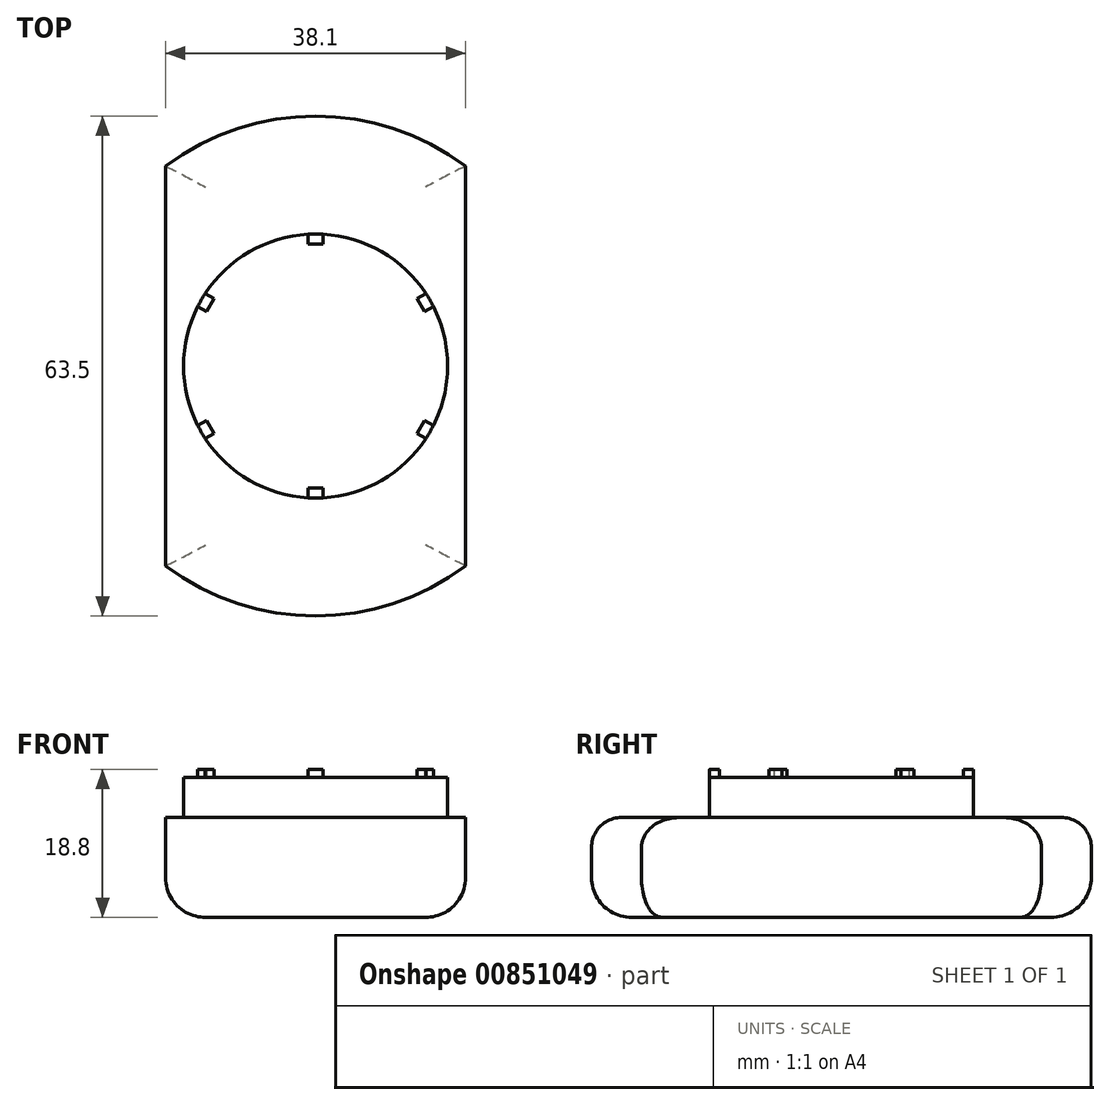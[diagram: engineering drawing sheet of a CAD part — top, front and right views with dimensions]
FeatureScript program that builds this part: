
annotation { "Feature Type Name" : "Feature", "Feature Type Description" : "" }
export const myFeature = defineFeature(function(context is Context, id is Id, definition is map)
    precondition{}
    {
        {
            var Q0;
            Q0=qCreatedBy(makeId("Top.planeOp"),FACE);
            var sketch = newSketch(context, id + "F0", { "sketchPlane" : qUnion([Q0])});
            skCircle(sketch, "E0", {"center": v(0, 0) * mm, "radius": 16.76 * mm});
            skLineSegment(sketch, "E1", {"start": v(-0.95, 16.74) * mm, "end": v(-0.95, 15.47) * mm});
            skLineSegment(sketch, "E2", {"start": v(-0.95, 15.47) * mm, "end": v(0.95, 15.47) * mm});
            skLineSegment(sketch, "E3", {"start": v(0.95, 15.47) * mm, "end": v(0.95, 16.74) * mm});
            skLineSegment(sketch, "E4", {"start": v(0, 0) * mm, "end": v(0, 15.47) * mm, "construction": true});
            skSolve(sketch);
        }
        {
            var Q0;
            Q0 = qSketchRegion(id + "F0", true);
            extrude(context, id + "F1", {"entities" : qUnion([Q0]), "oppositeDirection" : true, "depth" : 5.08 * mm, "offsetDistance" : 25.4 * mm});
        }
        {
            var Q0;
            {var subQ0=sQuery(id+"F0.wireOp",EDGE,"E1");Q0=makeQuery(id+"F0.imprint","IMPRINT",FACE,{"disambiguationData":[TD([[makeQuery(id+"F0.imprint","IMPRINT",EDGE,{"derivedFrom":subQ0}),1.0]])]});}
            extrude(context, id + "F2", {"entities" : qUnion([Q0]), "depth" : 1.02 * mm, "offsetDistance" : 25.4 * mm});
        }
        {
            var Q0;
            Q0=makeQuery(id+"F2.opExtrude","SWEPT_BODY",BODY,{"disambiguationData":[OSD([sQuery(id+"F0.wireOp",EDGE,"E0"),sQuery(id+"F0.wireOp",EDGE,"E1"),sQuery(id+"F0.wireOp",EDGE,"E2"),sQuery(id+"F0.wireOp",EDGE,"E3")])]});
            var Q1;
            Q1=sQuery(id+"F0.wireOp",EDGE,"E0");
            circularPattern(context, id + "F3", {"entities" : qUnion([Q0]), "axis" : qUnion([Q1]), "angle" : 360 * degree, "instanceCount" : 6, "equalSpace" : true});
        }
        {
            var Q0;
            Q0=makeQuery(id+"F1.opExtrude","CAP_FACE",FACE,{"disambiguationData":[OSD([sQuery(id+"F0.wireOp",EDGE,"E0")])],"isStart":false});
            var sketch = newSketch(context, id + "F4", { "sketchPlane" : qUnion([Q0])});
            skCircle(sketch, "E5", {"center": v(0, 0) * mm, "radius": 31.75 * mm});
            skLineSegment(sketch, "E6", {"start": v(-19.05, 25.4) * mm, "end": v(-19.05, -25.4) * mm});
            skLineSegment(sketch, "E7", {"start": v(19.05, 25.4) * mm, "end": v(19.05, -25.4) * mm});
            skSolve(sketch);
        }
        {
            var Q0;
            Q0=makeQuery(id+"F4.imprint","IMPRINT",FACE,{"disambiguationData":[TD([[makeQuery(id+"F4.imprint","IMPRINT",EDGE,{"derivedFrom":makeQuery(id+"F1.opExtrude","CAP_EDGE",EDGE,{"disambiguationData":[OSD([sQuery(id+"F0.wireOp",EDGE,"E0")])],"isStart":false})}),-1.0]])]});
            var Q1;
            {var subQ0=sQuery(id+"F4.wireOp",EDGE,"E6");Q1=makeQuery(id+"F4.imprint","IMPRINT",FACE,{"disambiguationData":[TD([[makeQuery(id+"F4.imprint","IMPRINT",EDGE,{"derivedFrom":subQ0}),1.0]])]});}
            extrude(context, id + "F5", {"entities" : qUnion([Q0, Q1]), "operationType" : NewBodyOperationType.ADD, "depth" : 12.7 * mm, "offsetDistance" : 25.4 * mm});
        }
        {
            var Q0;
            Q0=makeQuery(id+"F1.opExtrude","CAP_EDGE",EDGE,{"disambiguationData":[OSD([sQuery(id+"F0.wireOp",EDGE,"E0")])],"isStart":false});
            var Q1;
            Q1=makeQuery(id+"F5.opExtrude","CAP_EDGE",EDGE,{"disambiguationData":[OSD([sQuery(id+"F4.wireOp",EDGE,"E5")])],"isStart":true});
            fillet(context, id + "F6", {"entities" : qUnion([Q0, Q1]), "radius" : 3.8 * mm, "tangentPropagation" : true, "allowEdgeOverflow" : false});
        }
        {
            var Q0;
            Q0=makeQuery(id+"F5.opExtrude","CAP_EDGE",EDGE,{"disambiguationData":[OSD([sQuery(id+"F4.wireOp",EDGE,"E5")])],"isStart":false});
            var Q1;
            Q1=makeQuery(id+"F5.opExtrude","CAP_EDGE",EDGE,{"disambiguationData":[OSD([sQuery(id+"F4.wireOp",EDGE,"E7")])],"isStart":false});
            var Q2;
            Q2=makeQuery(id+"F5.opExtrude","CAP_EDGE",EDGE,{"disambiguationData":[OSD([sQuery(id+"F4.wireOp",EDGE,"E6")])],"isStart":false});
            fillet(context, id + "F7", {"entities" : qUnion([Q0, Q1, Q2]), "radius" : 5.08 * mm, "tangentPropagation" : true, "allowEdgeOverflow" : false});
        }
    });
